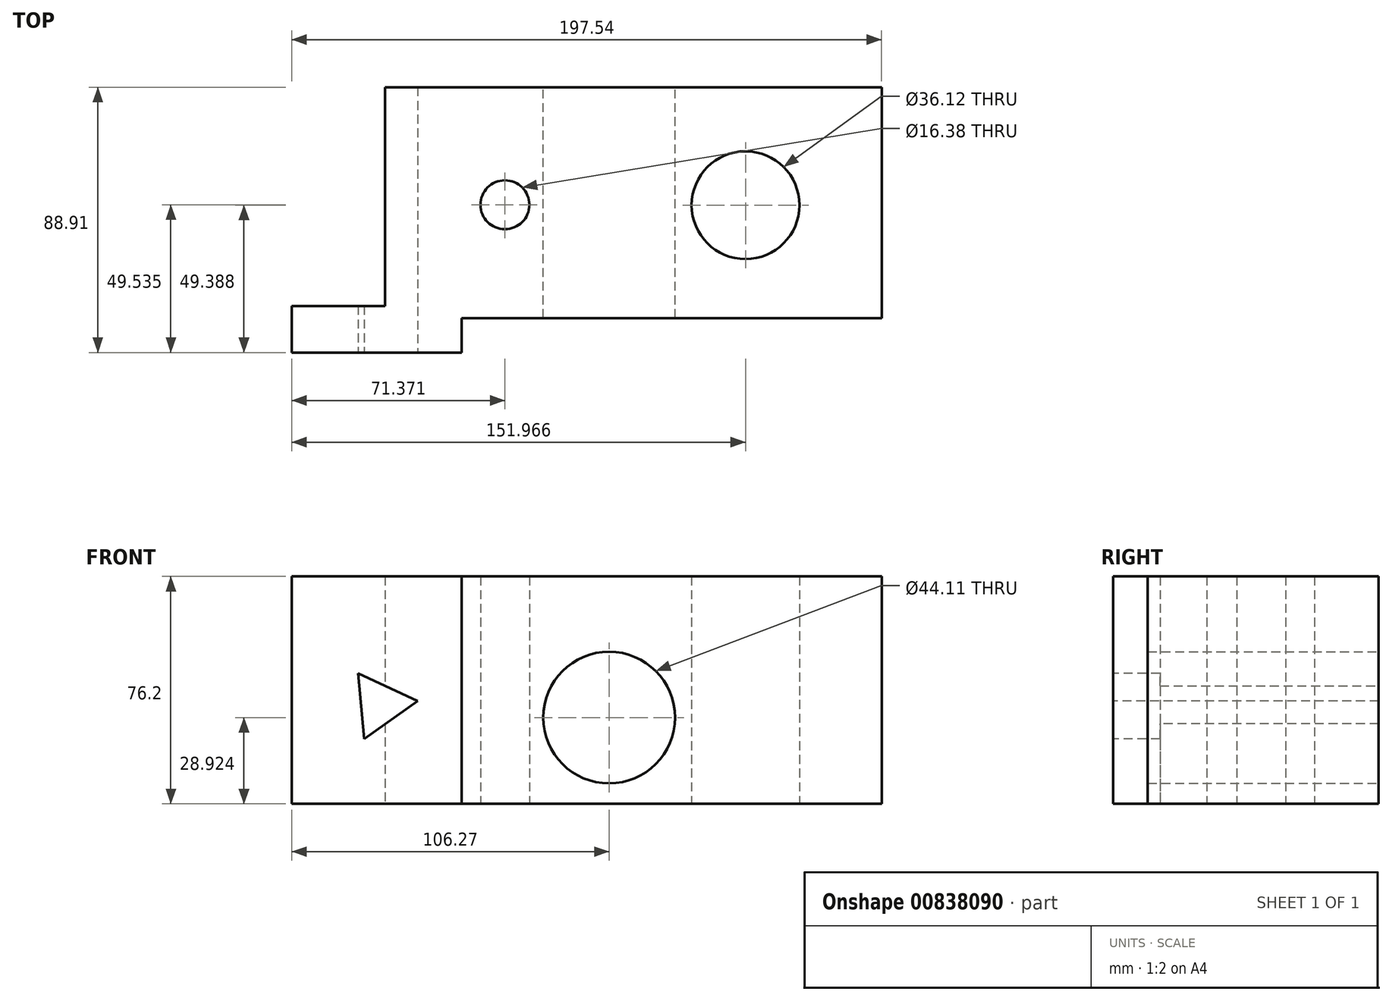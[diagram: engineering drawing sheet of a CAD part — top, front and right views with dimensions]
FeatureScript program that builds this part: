
annotation { "Feature Type Name" : "Feature", "Feature Type Description" : "" }
export const myFeature = defineFeature(function(context is Context, id is Id, definition is map)
    precondition{}
    {
        {
            var Q0;
            Q0=qCreatedBy(makeId("Top.planeOp"),FACE);
            var sketch = newSketch(context, id + "F0", { "sketchPlane" : qUnion([Q0])});
            skLineSegment(sketch, "E0.bottom", {"start": v(-74.98, 35.17) * mm, "end": v(91.27, 35.17) * mm});
            skLineSegment(sketch, "E0.top", {"start": v(-74.98, -42.18) * mm, "end": v(91.27, -42.18) * mm});
            skLineSegment(sketch, "E0.left", {"start": v(-74.98, 35.17) * mm, "end": v(-74.98, -42.18) * mm});
            skLineSegment(sketch, "E0.right", {"start": v(91.27, 35.17) * mm, "end": v(91.27, -42.18) * mm});
            skCircle(sketch, "E1", {"center": v(-34.9, -4.2) * mm, "radius": 8.2 * mm});
            skCircle(sketch, "E2", {"center": v(45.7, -4.35) * mm, "radius": 18.06 * mm});
            skLineSegment(sketch, "E3.bottom", {"start": v(-106.27, -38.08) * mm, "end": v(-49.36, -38.08) * mm});
            skLineSegment(sketch, "E3.top", {"start": v(-106.27, -53.74) * mm, "end": v(-49.36, -53.74) * mm});
            skLineSegment(sketch, "E3.left", {"start": v(-106.27, -38.08) * mm, "end": v(-106.27, -53.74) * mm});
            skLineSegment(sketch, "E3.right", {"start": v(-49.36, -38.08) * mm, "end": v(-49.36, -53.74) * mm});
            skSolve(sketch);
        }
        {
            var Q0;
            Q0=makeQuery(id+"F0.imprint","IMPRINT",FACE,{"disambiguationData":[TD([[makeQuery(id+"F0.imprint","IMPRINT",EDGE,{"derivedFrom":sQuery(id+"F0.wireOp",EDGE,"E0.bottom")}),-1.0]])]});
            var Q1;
            {var subQ0=sQuery(id+"F0.wireOp",EDGE,"E3.top");Q1=makeQuery(id+"F0.imprint","IMPRINT",FACE,{"disambiguationData":[TD([[makeQuery(id+"F0.imprint","IMPRINT",EDGE,{"derivedFrom":subQ0}),1.0]])]});}
            var Q2;
            {var subQ0=sQuery(id+"F0.wireOp",EDGE,"E0.left");var subQ1=sQuery(id+"F0.wireOp",EDGE,"E0.top");var subQ2=makeQuery(id+"F0.imprint","INTERSECT",VERTEX,{"derivedFrom":[subQ1,subQ0]});Q2=makeQuery(id+"F0.imprint","IMPRINT",FACE,{"disambiguationData":[TD([[makeQuery(id+"F0.imprint","IMPRINT",EDGE,{"disambiguationData":[TD([[subQ2,-1.0]])],"derivedFrom":subQ1}),1.0]])]});}
            extrude(context, id + "F1", {"entities" : qUnion([Q0, Q1, Q2]), "depth" : 76.2 * mm, "offsetDistance" : 25.4 * mm});
        }
        {
            var Q0;
            Q0=makeQuery(id+"F1.opExtrude","SWEPT_FACE",FACE,{"disambiguationData":[OSD([sQuery(id+"F0.wireOp",EDGE,"E3.top")])]});
            var sketch = newSketch(context, id + "F2", { "sketchPlane" : qUnion([Q0])});
            skCircle(sketch, "E4.cCircle", {"center": v(-76.74, 33.36) * mm, "radius": 6.35 * mm, "construction": true});
            skLineSegment(sketch, "E4.0", {"start": v(-84.07, 43.73) * mm, "end": v(-64.1, 34.53) * mm});
            skLineSegment(sketch, "E4.1", {"start": v(-64.1, 34.53) * mm, "end": v(-82.06, 21.83) * mm});
            skLineSegment(sketch, "E4.2", {"start": v(-82.06, 21.83) * mm, "end": v(-84.07, 43.73) * mm});
            skPoint(sketch, "E4.0.midPoint", {"position": v(-74.08, 39.13) * mm});
            skSolve(sketch);
        }
        {
            var Q0;
            Q0=makeQuery(id+"F2.imprint","IMPRINT",FACE,{"disambiguationData":[TD([[makeQuery(id+"F2.imprint","IMPRINT",EDGE,{"derivedFrom":sQuery(id+"F2.wireOp",EDGE,"E4.0")}),-1.0]])]});
            extrude(context, id + "F3", {"entities" : qUnion([Q0]), "operationType" : NewBodyOperationType.REMOVE, "endBound" : BoundingType.THROUGH_ALL, "oppositeDirection" : true, "depth" : 25.4 * mm, "offsetDistance" : 25.4 * mm});
        }
        {
            var Q0;
            Q0=makeQuery(id+"F1.opExtrude","SWEPT_FACE",FACE,{"disambiguationData":[OSD([sQuery(id+"F0.wireOp",EDGE,"E0.bottom")])]});
            var sketch = newSketch(context, id + "F4", { "sketchPlane" : qUnion([Q0])});
            skCircle(sketch, "E5", {"center": v(0, 28.92) * mm, "radius": 22.06 * mm});
            skSolve(sketch);
        }
        {
            var Q0;
            Q0=makeQuery(id+"F4.imprint","IMPRINT",FACE,{"disambiguationData":[TD([[makeQuery(id+"F4.imprint","IMPRINT",EDGE,{"derivedFrom":sQuery(id+"F4.wireOp",EDGE,"E5")}),1.0]])]});
            extrude(context, id + "F5", {"entities" : qUnion([Q0]), "operationType" : NewBodyOperationType.REMOVE, "endBound" : BoundingType.THROUGH_ALL, "oppositeDirection" : true, "depth" : 25.4 * mm, "offsetDistance" : 25.4 * mm});
        }
    });
